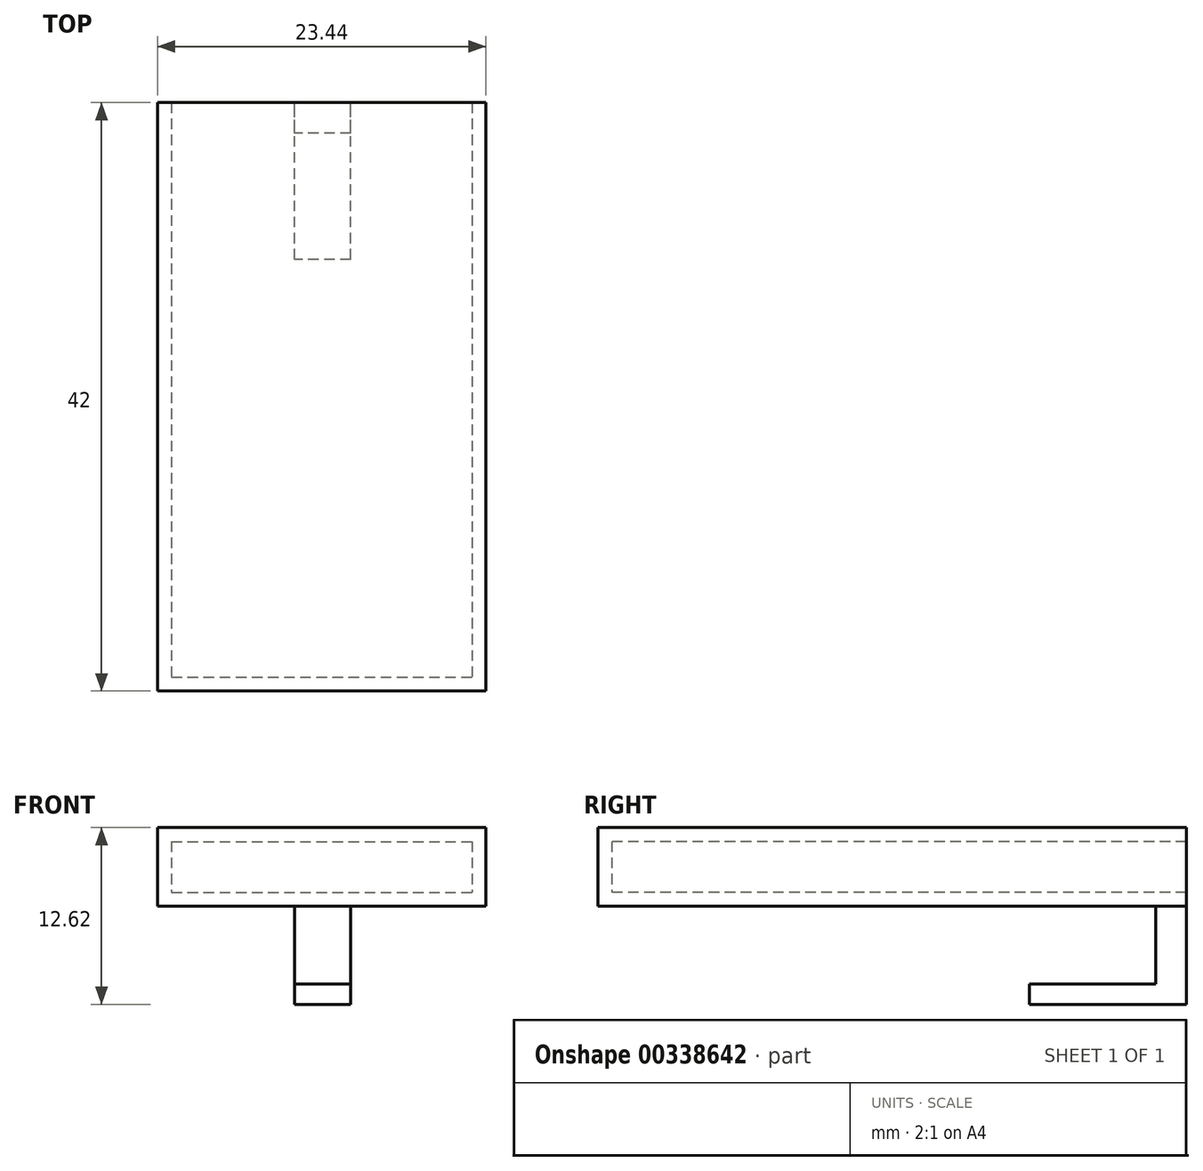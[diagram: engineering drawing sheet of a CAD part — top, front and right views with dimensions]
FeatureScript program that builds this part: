
annotation { "Feature Type Name" : "Feature", "Feature Type Description" : "" }
export const myFeature = defineFeature(function(context is Context, id is Id, definition is map)
    precondition{}
    {
        {
            var Q0;
            Q0=qCreatedBy(makeId("Top.planeOp"),FACE);
            var sketch = newSketch(context, id + "F0", { "sketchPlane" : qUnion([Q0])});
            skLineSegment(sketch, "E0.bottom", {"start": v(-11.73, 21) * mm, "end": v(11.72, 21) * mm});
            skLineSegment(sketch, "E0.top", {"start": v(-11.72, -21) * mm, "end": v(11.72, -21) * mm});
            skLineSegment(sketch, "E0.left", {"start": v(-11.72, 21) * mm, "end": v(-11.73, -21) * mm});
            skLineSegment(sketch, "E0.right", {"start": v(11.73, 21) * mm, "end": v(11.72, -21) * mm});
            skPoint(sketch, "E0.middle", {"position": v(0, 0) * mm});
            skSolve(sketch);
        }
        {
            var Q0;
            Q0 = qSketchRegion(id + "F0", true);
            extrude(context, id + "F1", {"entities" : qUnion([Q0]), "depth" : 5.63 * mm});
        }
        {
            var Q0;
            Q0=makeQuery(id+"F1.opExtrude","SWEPT_FACE",FACE,{"disambiguationData":[OSD([sQuery(id+"F0.wireOp",EDGE,"E0.bottom")])]});
            var Q1;
            Q1=makeQuery(id+"F1.opExtrude","SWEPT_BODY",BODY,{"disambiguationData":[OSD([sQuery(id+"F0.wireOp",EDGE,"E0.bottom"),sQuery(id+"F0.wireOp",EDGE,"E0.top"),sQuery(id+"F0.wireOp",EDGE,"E0.left"),sQuery(id+"F0.wireOp",EDGE,"E0.right")])]});
            shell(context, id + "F2", {"entities" : qUnion([Q0]), "parts" : qUnion([Q1]), "thickness" : 1 * mm});
        }
        {
            var Q0;
            Q0=makeQuery(id+"F1.opExtrude","SWEPT_FACE",FACE,{"disambiguationData":[OSD([sQuery(id+"F0.wireOp",EDGE,"E0.bottom")])]});
            var sketch = newSketch(context, id + "F3", { "sketchPlane" : qUnion([Q0])});
            skLineSegment(sketch, "E1.bottom", {"start": v(-2.08, 0) * mm, "end": v(1.92, 0) * mm});
            skLineSegment(sketch, "E1.top", {"start": v(-2.08, -6.99) * mm, "end": v(1.92, -6.99) * mm});
            skLineSegment(sketch, "E1.left", {"start": v(-2.08, 0) * mm, "end": v(-2.08, -6.99) * mm});
            skLineSegment(sketch, "E1.right", {"start": v(1.92, 0) * mm, "end": v(1.92, -6.99) * mm});
            skSolve(sketch);
        }
        {
            var Q0;
            Q0 = qSketchRegion(id + "F3", true);
            extrude(context, id + "F4", {"entities" : qUnion([Q0]), "operationType" : NewBodyOperationType.ADD, "oppositeDirection" : true, "depth" : 2.2 * mm});
        }
        {
            var Q0;
            Q0=makeQuery(id+"F4.opExtrude","CAP_FACE",FACE,{"disambiguationData":[OSD([sQuery(id+"F3.wireOp",EDGE,"E1.bottom"),sQuery(id+"F3.wireOp",EDGE,"E1.top"),sQuery(id+"F3.wireOp",EDGE,"E1.left"),sQuery(id+"F3.wireOp",EDGE,"E1.right")])],"isStart":false});
            var sketch = newSketch(context, id + "F5", { "sketchPlane" : qUnion([Q0])});
            skLineSegment(sketch, "E2.bottom", {"start": v(2.08, -6.99) * mm, "end": v(-1.92, -6.99) * mm});
            skLineSegment(sketch, "E2.top", {"start": v(2.08, -5.53) * mm, "end": v(-1.92, -5.53) * mm});
            skLineSegment(sketch, "E2.left", {"start": v(2.08, -6.99) * mm, "end": v(2.08, -5.53) * mm});
            skLineSegment(sketch, "E2.right", {"start": v(-1.92, -6.99) * mm, "end": v(-1.92, -5.53) * mm});
            skSolve(sketch);
        }
        {
            var Q0;
            Q0=makeQuery(id+"F5.imprint","IMPRINT",FACE,{"disambiguationData":[TD([[makeQuery(id+"F5.imprint","IMPRINT",EDGE,{"derivedFrom":sQuery(id+"F5.wireOp",EDGE,"E2.bottom")}),-1.0]])]});
            extrude(context, id + "F6", {"entities" : qUnion([Q0]), "operationType" : NewBodyOperationType.ADD, "depth" : 9 * mm});
        }
    });
